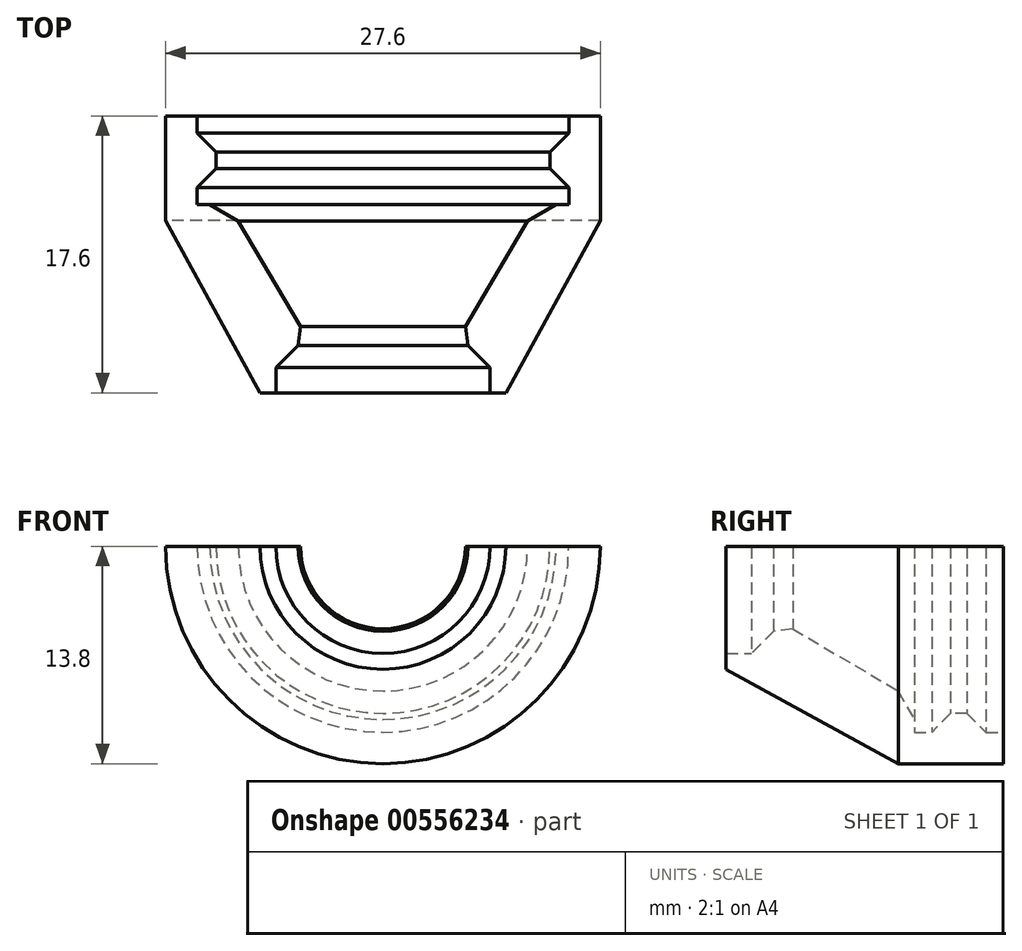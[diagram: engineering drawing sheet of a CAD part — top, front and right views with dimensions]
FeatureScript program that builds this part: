
annotation { "Feature Type Name" : "Feature", "Feature Type Description" : "" }
export const myFeature = defineFeature(function(context is Context, id is Id, definition is map)
    precondition{}
    {
        {
            var Q0;
            Q0=qCreatedBy(makeId("Top.planeOp"),FACE);
            var sketch = newSketch(context, id + "F0", { "sketchPlane" : qUnion([Q0])});
            skLineSegment(sketch, "E0", {"start": v(-11.8, 6.65) * mm, "end": v(-11.8, 5.65) * mm});
            skLineSegment(sketch, "E1", {"start": v(-11.8, 5.65) * mm, "end": v(-9.8, 5.65) * mm});
            skLineSegment(sketch, "E2", {"start": v(-9.8, 2) * mm, "end": v(-11.8, 2) * mm});
            skLineSegment(sketch, "E3", {"start": v(-11.8, 2) * mm, "end": v(-11.8, 1) * mm});
            skLineSegment(sketch, "E4", {"start": v(-11.8, 1) * mm, "end": v(-9.8, 1) * mm});
            skLineSegment(sketch, "E5", {"start": v(-4.8, -9.45) * mm, "end": v(-6.8, -9.45) * mm});
            skLineSegment(sketch, "E6", {"start": v(-6.8, -9.45) * mm, "end": v(-6.8, -10.95) * mm});
            skLineSegment(sketch, "E7", {"start": v(0, 15) * mm, "end": v(0, -15) * mm});
            skLineSegment(sketch, "E8", {"start": v(-9.8, 2) * mm, "end": v(-9.8, 5.65) * mm});
            skLineSegment(sketch, "E9", {"start": v(-13.8, 6.65) * mm, "end": v(-13.8, 0) * mm});
            skLineSegment(sketch, "E10", {"start": v(-13.8, 0) * mm, "end": v(-7.8, -10.95) * mm});
            skLineSegment(sketch, "E11", {"start": v(-4.8, -9.45) * mm, "end": v(-4.8, -7.45) * mm});
            skLineSegment(sketch, "E12", {"start": v(-7.8, -10.95) * mm, "end": v(-6.8, -10.95) * mm});
            skLineSegment(sketch, "E13", {"start": v(-11.8, 6.65) * mm, "end": v(-13.8, 6.65) * mm});
            skLineSegment(sketch, "E14", {"start": v(-9.8, 1) * mm, "end": v(-4.8, -7.45) * mm});
            skSolve(sketch);
        }
        {
            var Q0;
            Q0=makeQuery(id+"F0.imprint","IMPRINT",FACE,{"disambiguationData":[TD([[makeQuery(id+"F0.imprint","IMPRINT",EDGE,{"derivedFrom":sQuery(id+"F0.wireOp",EDGE,"E0")}),-1.0]])]});
            var Q1;
            Q1=makeQuery(id+"F0.imprint","IMPRINT",FACE,{"disambiguationData":[TD([[makeQuery(id+"F0.imprint","IMPRINT",EDGE,{"derivedFrom":sQuery(id+"F0.wireOp",EDGE,"WN2nG1eU-nUzO-fPRU-tTYX-om5CcBassxre.top")}),-1.0]])]});
            var Q2;
            Q2=sQuery(id+"F0.wireOp",EDGE,"E7");
            revolve(context, id + "F1", {"entities" : qUnion([Q0, Q1]), "axis" : qUnion([Q2]), "revolveType" : RevolveType.ONE_DIRECTION, "angle" : 180 * degree});
        }
        {
            var Q0;
            Q0=makeQuery(id+"F1.opRevolve","SWEPT_EDGE",EDGE,{"disambiguationData":[OSD([sQuery(id+"F0.wireOp",EDGE,"E1"),sQuery(id+"F0.wireOp",EDGE,"E8")])]});
            chamfer(context, id + "F2", {"entities" : qUnion([Q0]), "width" : 2.1 * mm, "tangentPropagation" : true});
        }
        {
            var Q0;
            Q0=makeQuery(id+"F1.opRevolve","SWEPT_EDGE",EDGE,{"disambiguationData":[OSD([sQuery(id+"F0.wireOp",EDGE,"E4"),sQuery(id+"F0.wireOp",EDGE,"E14")])]});
            chamfer(context, id + "F3", {"entities" : qUnion([Q0]), "width" : 2.1 * mm, "tangentPropagation" : true});
        }
        {
            var Q0;
            Q0=makeQuery(id+"F1.opRevolve","SWEPT_EDGE",EDGE,{"disambiguationData":[OSD([sQuery(id+"F0.wireOp",EDGE,"E5"),sQuery(id+"F0.wireOp",EDGE,"E11")])]});
            var Q1;
            Q1=makeQuery(id+"F1.opRevolve","SWEPT_EDGE",EDGE,{"disambiguationData":[OSD([sQuery(id+"F0.wireOp",EDGE,"E2"),sQuery(id+"F0.wireOp",EDGE,"E8")])]});
            chamfer(context, id + "F4", {"entities" : qUnion([Q0, Q1]), "width" : 2.1 * mm, "tangentPropagation" : true});
        }
        {
            var Q0;
            {var subQ0=sQuery(id+"F0.wireOp",EDGE,"E8");Q0=makeQuery(id+"F4.opChamfer","BLEND_EDGE",EDGE,{"blendedFrom":[makeQuery(id+"F1.opRevolve","SWEPT_EDGE",EDGE,{"disambiguationData":[OSD([sQuery(id+"F0.wireOp",EDGE,"E2"),subQ0])]}),makeQuery(id+"F2.opChamfer","BLEND_FACE",FACE,{"disambiguationData":[OSD([sQuery(id+"F0.wireOp",EDGE,"E1"),subQ0])]})],"blendedInto":[makeQuery(id+"F2.opChamfer","BLEND_FACE",FACE,{"disambiguationData":[OSD([sQuery(id+"F0.wireOp",EDGE,"E1"),subQ0])]})]});}
            chamfer(context, id + "F5", {"entities" : qUnion([Q0]), "width" : 0.75 * mm, "tangentPropagation" : true});
        }
        {
            var Q0;
            Q0=makeQuery(id+"F4.opChamfer","BLEND_EDGE",EDGE,{"blendedFrom":[makeQuery(id+"F1.opRevolve","SWEPT_EDGE",EDGE,{"disambiguationData":[OSD([sQuery(id+"F0.wireOp",EDGE,"E5"),sQuery(id+"F0.wireOp",EDGE,"E11")])]}),makeQuery(id+"F1.opRevolve","SWEPT_FACE",FACE,{"disambiguationData":[OSD([sQuery(id+"F0.wireOp",EDGE,"E14")])]})],"blendedInto":[makeQuery(id+"F1.opRevolve","SWEPT_FACE",FACE,{"disambiguationData":[OSD([sQuery(id+"F0.wireOp",EDGE,"E14")])]})]});
            chamfer(context, id + "F6", {"entities" : qUnion([Q0]), "width" : 1 * mm, "tangentPropagation" : true});
        }
    });
